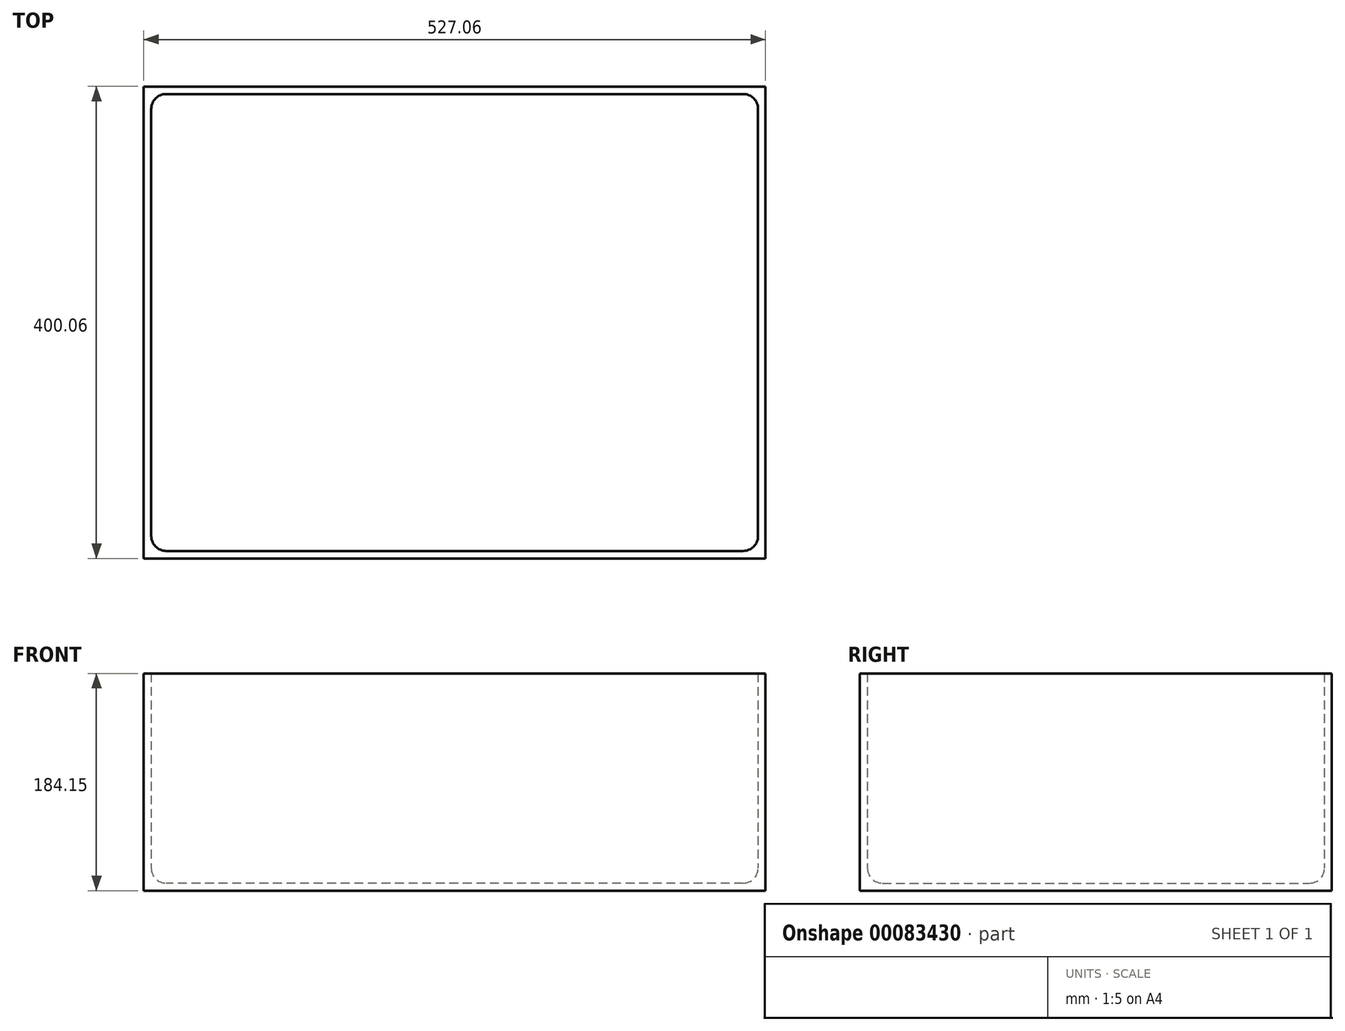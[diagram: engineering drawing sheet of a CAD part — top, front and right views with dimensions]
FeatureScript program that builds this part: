
annotation { "Feature Type Name" : "Feature", "Feature Type Description" : "" }
export const myFeature = defineFeature(function(context is Context, id is Id, definition is map)
    precondition{}
    {
        {
            var Q0;
            Q0=qCreatedBy(makeId("Top.planeOp"),FACE);
            var sketch = newSketch(context, id + "F0", { "sketchPlane" : qUnion([Q0])});
            skLineSegment(sketch, "E0.bottom", {"start": v(257.18, -193.67) * mm, "end": v(-257.18, -193.68) * mm});
            skLineSegment(sketch, "E0.top", {"start": v(257.18, 193.68) * mm, "end": v(-257.18, 193.68) * mm});
            skLineSegment(sketch, "E0.left", {"start": v(257.18, -193.67) * mm, "end": v(257.18, 193.68) * mm});
            skLineSegment(sketch, "E0.right", {"start": v(-257.18, -193.68) * mm, "end": v(-257.18, 193.68) * mm});
            skPoint(sketch, "E0.middle", {"position": v(0, 0) * mm});
            skLineSegment(sketch, "E1.0", {"start": v(-263.53, -200.03) * mm, "end": v(-263.53, 200.03) * mm});
            skLineSegment(sketch, "E1.1", {"start": v(263.53, -200.02) * mm, "end": v(-263.53, -200.03) * mm});
            skLineSegment(sketch, "E1.2", {"start": v(263.53, -200.02) * mm, "end": v(263.53, 200.03) * mm});
            skLineSegment(sketch, "E1.3", {"start": v(263.53, 200.03) * mm, "end": v(-263.53, 200.03) * mm});
            skSolve(sketch);
        }
        {
            var Q0;
            Q0 = qSketchRegion(id + "F0", true);
            extrude(context, id + "F1", {"entities" : qUnion([Q0]), "depth" : 177.8 * mm});
        }
        {
            var Q0;
            Q0=makeQuery(id+"F1.opExtrude","CAP_FACE",FACE,{"disambiguationData":[OSD([sQuery(id+"F0.wireOp",EDGE,"E0.bottom"),sQuery(id+"F0.wireOp",EDGE,"E0.top"),sQuery(id+"F0.wireOp",EDGE,"E0.left"),sQuery(id+"F0.wireOp",EDGE,"E0.right"),sQuery(id+"F0.wireOp",EDGE,"E1.0"),sQuery(id+"F0.wireOp",EDGE,"E1.1"),sQuery(id+"F0.wireOp",EDGE,"E1.2"),sQuery(id+"F0.wireOp",EDGE,"E1.3")])],"isStart":true});
            var sketch = newSketch(context, id + "F2", { "sketchPlane" : qUnion([Q0])});
            skLineSegment(sketch, "E2.bottom", {"start": v(-263.53, 200.03) * mm, "end": v(263.53, 200.03) * mm});
            skLineSegment(sketch, "E2.top", {"start": v(-263.53, -200.03) * mm, "end": v(263.53, -200.03) * mm});
            skLineSegment(sketch, "E2.left", {"start": v(-263.53, 200.03) * mm, "end": v(-263.53, -200.03) * mm});
            skLineSegment(sketch, "E2.right", {"start": v(263.53, 200.03) * mm, "end": v(263.53, -200.03) * mm});
            skSolve(sketch);
        }
        {
            var Q0;
            Q0 = qSketchRegion(id + "F2", true);
            extrude(context, id + "F3", {"entities" : qUnion([Q0]), "operationType" : NewBodyOperationType.ADD, "depth" : 6.35 * mm});
        }
        {
            var Q0;
            Q0=makeQuery(id+"F3.opExtrude","CAP_FACE",FACE,{"disambiguationData":[OSD([sQuery(id+"F2.wireOp",EDGE,"E2.bottom"),sQuery(id+"F2.wireOp",EDGE,"E2.top"),sQuery(id+"F2.wireOp",EDGE,"E2.left"),sQuery(id+"F2.wireOp",EDGE,"E2.right")])],"isStart":true});
            var Q1;
            Q1=makeQuery(id+"F1.opExtrude","SWEPT_EDGE",EDGE,{"disambiguationData":[OSD([sQuery(id+"F0.wireOp",EDGE,"E0.top"),sQuery(id+"F0.wireOp",EDGE,"E0.right")])]});
            var Q2;
            Q2=makeQuery(id+"F1.opExtrude","SWEPT_EDGE",EDGE,{"disambiguationData":[OSD([sQuery(id+"F0.wireOp",EDGE,"E0.bottom"),sQuery(id+"F0.wireOp",EDGE,"E0.right")])]});
            var Q3;
            Q3=makeQuery(id+"F1.opExtrude","SWEPT_EDGE",EDGE,{"disambiguationData":[OSD([sQuery(id+"F0.wireOp",EDGE,"E0.bottom"),sQuery(id+"F0.wireOp",EDGE,"E0.left")])]});
            var Q4;
            Q4=makeQuery(id+"F1.opExtrude","SWEPT_EDGE",EDGE,{"disambiguationData":[OSD([sQuery(id+"F0.wireOp",EDGE,"E0.top"),sQuery(id+"F0.wireOp",EDGE,"E0.left")])]});
            fillet(context, id + "F4", {"entities" : qUnion([Q0, Q1, Q2, Q3, Q4]), "radius" : 12.7 * mm, "tangentPropagation" : true, "allowEdgeOverflow" : false});
        }
    });
